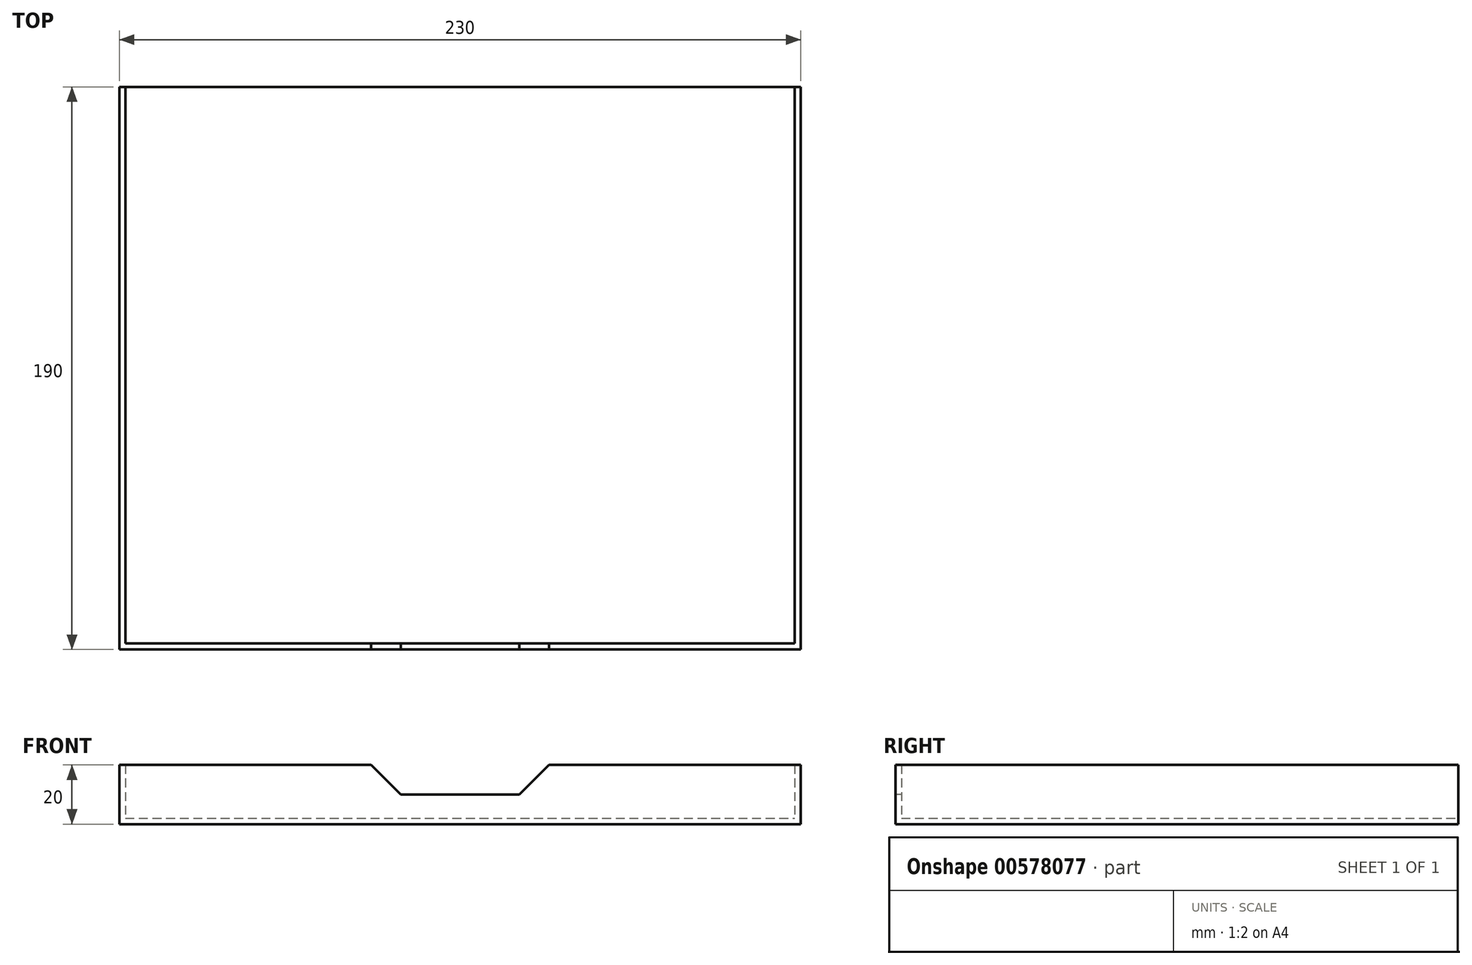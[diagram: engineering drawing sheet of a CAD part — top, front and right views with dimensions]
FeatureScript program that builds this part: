
annotation { "Feature Type Name" : "Feature", "Feature Type Description" : "" }
export const myFeature = defineFeature(function(context is Context, id is Id, definition is map)
    precondition{}
    {
        {
            var Q0;
            Q0=qCreatedBy(makeId("Front.planeOp"),FACE);
            var sketch = newSketch(context, id + "F0", { "sketchPlane" : qUnion([Q0])});
            skLineSegment(sketch, "E0.top", {"start": v(-115, -10) * mm, "end": v(115, -10) * mm});
            skLineSegment(sketch, "E0.left", {"start": v(-115, 10) * mm, "end": v(-115, -10) * mm});
            skLineSegment(sketch, "E0.right", {"start": v(115, 10) * mm, "end": v(115, -10) * mm});
            skPoint(sketch, "E0.middle", {"position": v(0, 0) * mm});
            skLineSegment(sketch, "E1.0", {"start": v(-113, 10) * mm, "end": v(-113, -8) * mm});
            skLineSegment(sketch, "E2.0", {"start": v(113, 10) * mm, "end": v(113, -8) * mm});
            skLineSegment(sketch, "E3.0", {"start": v(-113, -8) * mm, "end": v(113, -8) * mm});
            skLineSegment(sketch, "E4", {"start": v(-113, 10) * mm, "end": v(-115, 10) * mm});
            skLineSegment(sketch, "E5", {"start": v(113, 10) * mm, "end": v(115, 10) * mm});
            skSolve(sketch);
        }
        {
            var Q0;
            Q0=qSketchRegion(id+"F0",true);
            extrude(context, id + "F1", {"entities" : qUnion([Q0]), "depth" : 190 * mm, "offsetDistance" : 25 * mm});
        }
        {
            var Q0;
            Q0=makeQuery(id+"F1.opExtrude","CAP_FACE",FACE,{"disambiguationData":[OSD([sQuery(id+"F0.wireOp",EDGE,"E0.top"),sQuery(id+"F0.wireOp",EDGE,"E0.left"),sQuery(id+"F0.wireOp",EDGE,"E0.right"),sQuery(id+"F0.wireOp",EDGE,"E1.0"),sQuery(id+"F0.wireOp",EDGE,"E2.0"),sQuery(id+"F0.wireOp",EDGE,"E3.0"),sQuery(id+"F0.wireOp",EDGE,"E4"),sQuery(id+"F0.wireOp",EDGE,"E5")])],"isStart":false});
            var sketch = newSketch(context, id + "F2", { "sketchPlane" : qUnion([Q0])});
            skLineSegment(sketch, "E6.0", {"start": v(-115, 10) * mm, "end": v(-115, -10) * mm});
            skLineSegment(sketch, "E7.0", {"start": v(-115, -10) * mm, "end": v(115, -10) * mm});
            skLineSegment(sketch, "E8.0", {"start": v(115, 10) * mm, "end": v(115, -10) * mm});
            skLineSegment(sketch, "E9", {"start": v(115, 10) * mm, "end": v(-115, 10) * mm});
            skSolve(sketch);
        }
        {
            var Q0;
            Q0=qSketchRegion(id+"F2",true);
            extrude(context, id + "F3", {"entities" : qUnion([Q0]), "operationType" : NewBodyOperationType.ADD, "oppositeDirection" : true, "depth" : 2 * mm, "offsetDistance" : 25 * mm});
        }
        {
            var Q0;
            Q0=qCreatedBy(makeId("Front.planeOp"),FACE);
            cPlane(context, id + "F4", {"entities" : qUnion([Q0]), "cplaneType" : CPlaneType.OFFSET, "offset" : 95 * mm, "width" : 150 * mm, "height" : 150 * mm});
        }
        {
            var Q0;
            Q0=makeQuery(id+"F3.boolean.opBoolean","MERGE",FACE,{"derivedFrom":[makeQuery(id+"F1.opExtrude","CAP_FACE",FACE,{"disambiguationData":[OSD([sQuery(id+"F0.wireOp",EDGE,"E0.top"),sQuery(id+"F0.wireOp",EDGE,"E0.left"),sQuery(id+"F0.wireOp",EDGE,"E0.right"),sQuery(id+"F0.wireOp",EDGE,"E1.0"),sQuery(id+"F0.wireOp",EDGE,"E2.0"),sQuery(id+"F0.wireOp",EDGE,"E3.0"),sQuery(id+"F0.wireOp",EDGE,"E4"),sQuery(id+"F0.wireOp",EDGE,"E5")])],"isStart":false}),makeQuery(id+"F3.opExtrude","CAP_FACE",FACE,{"disambiguationData":[OSD([sQuery(id+"F2.wireOp",EDGE,"E6.0"),sQuery(id+"F2.wireOp",EDGE,"E7.0"),sQuery(id+"F2.wireOp",EDGE,"E8.0"),sQuery(id+"F2.wireOp",EDGE,"E9")])],"isStart":true})]});
            var sketch = newSketch(context, id + "F5", { "sketchPlane" : qUnion([Q0])});
            skLineSegment(sketch, "E10", {"start": v(0, 0) * mm, "end": v(20, 0) * mm});
            skLineSegment(sketch, "E11", {"start": v(0, 0) * mm, "end": v(-20, 0) * mm});
            skLineSegment(sketch, "E12", {"start": v(0, 10) * mm, "end": v(30, 10) * mm});
            skLineSegment(sketch, "E13", {"start": v(30, 10) * mm, "end": v(20, 0) * mm});
            skLineSegment(sketch, "E14", {"start": v(0, 10) * mm, "end": v(-30, 10) * mm});
            skLineSegment(sketch, "E15", {"start": v(-30, 10) * mm, "end": v(-20, 0) * mm});
            skSolve(sketch);
        }
        {
            var Q0;
            Q0 = qSketchRegion(id + "F5", true);
            extrude(context, id + "F6", {"entities" : qUnion([Q0]), "operationType" : NewBodyOperationType.REMOVE, "endBound" : BoundingType.THROUGH_ALL, "oppositeDirection" : true, "depth" : 25 * mm, "offsetDistance" : 25 * mm});
        }
    });
